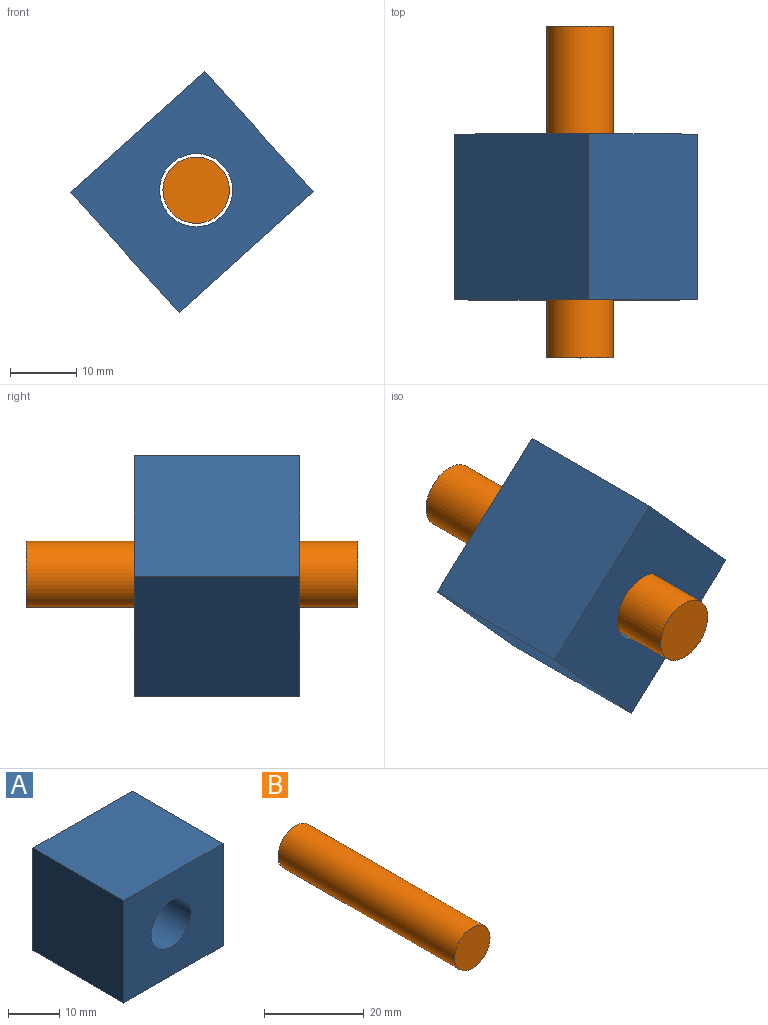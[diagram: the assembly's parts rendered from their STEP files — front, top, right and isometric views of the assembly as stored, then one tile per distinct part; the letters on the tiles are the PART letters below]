
ASSEMBLY  parts=2 mates=1
PART A: 7 faces, bbox 27.2x25x24.3 mm
  f0: plane 27.21x25mm, normal (0,0,1), area 680.1mm2, adj f1,f3,f4,f5
  f1: plane 25x24.34mm, normal (-1,0,0), area 608.6mm2, adj f0,f2,f4,f5
  f2: plane 27.21x25mm, normal (0,0,-1), area 680.1mm2, adj f1,f3,f4,f5
  f3: plane 25x24.34mm, normal (1,0,0), area 608.6mm2, adj f0,f2,f4,f5
  f4: plane 27.21x24.34mm, normal (0,-1,0), area 567.2mm2, adj f0,f1,f2,f3,f6
  f5: plane 27.21x24.34mm, normal (0,1,0), area 567.2mm2, adj f0,f1,f2,f3,f6
  f6: cylinder r=5.5mm len=25mm, axis (0,-1,0), area 863.9mm2, adj f4,f5
PART B: 3 faces, bbox 10x50x10 mm
  f0: cylinder r=5mm len=50mm, axis (0,1,0), area 1570.8mm2, adj f1,f2
  f1: plane 10x10mm, normal (0,1,0), area 78.5mm2, adj f0
  f2: plane 10x10mm, normal (0,-1,0), area 78.5mm2, adj f0
PLACE A rot(axis=(0,1,0),137.9deg) t=(-11.79,-22.29,0.83)mm
PLACE B t=(-11.79,-6.03,0.83)mm fixed
MATE cylindrical B.f0 <-> A.f6  axis (0,1,0) through (-11.79,-6.03,0.83)mm
